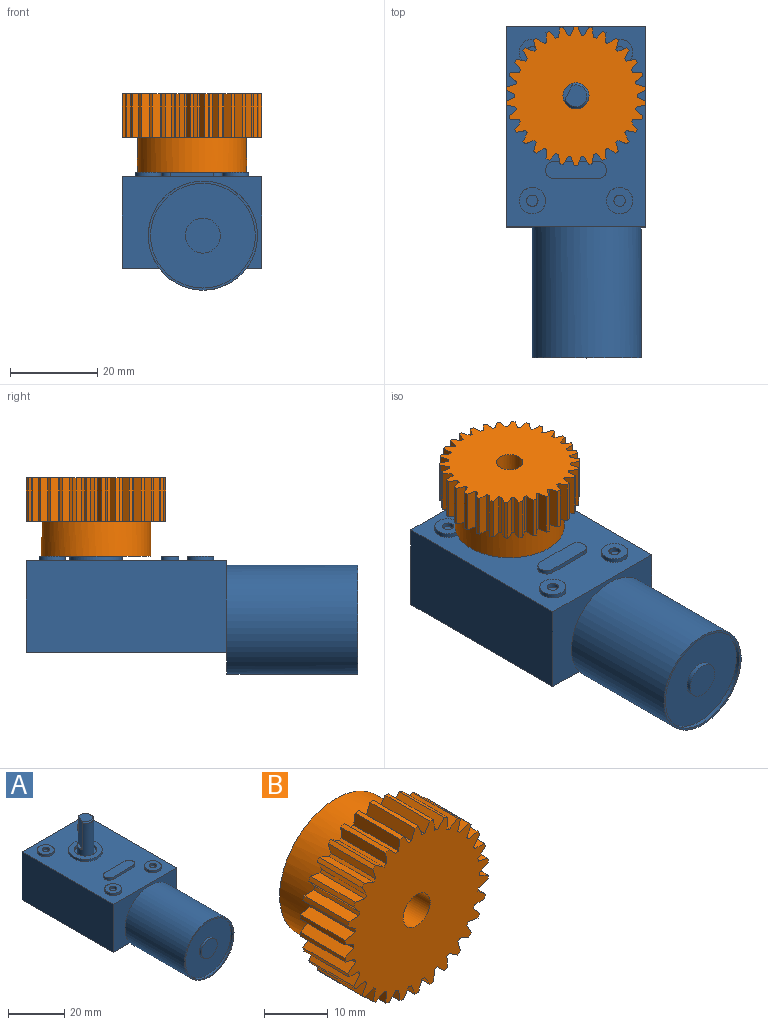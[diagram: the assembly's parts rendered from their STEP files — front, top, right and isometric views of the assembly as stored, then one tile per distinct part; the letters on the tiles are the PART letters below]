
ASSEMBLY  parts=2 mates=1
PART A: 43 faces, bbox 32.1x76.1x41.1 mm
  f0: plane 5x4.91mm, normal (0,0,1), area 18.3mm2, adj f1,f41
  f1: cone r=2.5mm half-angle=45deg, axis (0,0,-1), area 9.1mm2, adj f0,f40,f41
  f2: plane 46x32mm, normal (0,0,1), area 1193.2mm2, adj f10,f11,f13,f14,f16,f20,f24,f28
  f3: cylinder r=12.5mm len=30mm, axis (0,1,0), area 2356.2mm2, adj f4,f5,f10
  f4: plane 25x25mm, normal (0,-1,0), area 38.5mm2, adj f3,f7
  f5: plane 20x5mm, normal (0,1,0), area 69.9mm2, adj f3,f12
  f6: cylinder r=4mm len=8mm, axis (0,-1,0), area 25.1mm2, adj f8,f9
  f7: cylinder r=12mm len=24mm, axis (0,-1,0), area 75.4mm2, adj f4,f8
  f8: plane 24x24mm, normal (0,-1,0), area 402.1mm2, adj f6,f7
  f9: plane 8x8mm, normal (0,-1,0), area 50.3mm2, adj f6
  f10: plane 32x21mm, normal (0,-1,0), area 251mm2, adj f2,f3,f11,f12,f13
  f11: plane 46x21mm, normal (-1,0,0), area 966mm2, adj f2,f10,f12,f14
  f12: plane 46x32mm, normal (0,0,-1), area 1472mm2, adj f5,f10,f11,f13,f14
  f13: plane 46x21mm, normal (1,0,0), area 966mm2, adj f2,f10,f12,f14
  f14: plane 32x21mm, normal (0,1,0), area 672mm2, adj f2,f11,f12,f13
  f15: cylinder r=1.3mm len=2.6mm, axis (0,0,-1), area 8.2mm2, adj f17,f18
  f16: cylinder r=3mm len=6mm, axis (0,0,-1), area 18.8mm2, adj f2,f17
  f17: plane 6x6mm, normal (0,0,1), area 23mm2, adj f15,f16
  f18: plane 2.6x2.6mm, normal (0,0,1), area 5.3mm2, adj f15
  f19: cylinder r=1.3mm len=2.6mm, axis (0,0,-1), area 8.2mm2, adj f21,f22
  f20: cylinder r=3mm len=6mm, axis (0,0,-1), area 18.8mm2, adj f2,f21
  f21: plane 6x6mm, normal (0,0,1), area 23mm2, adj f19,f20
  f22: plane 2.6x2.6mm, normal (0,0,1), area 5.3mm2, adj f19
  f23: cylinder r=1.3mm len=2.6mm, axis (0,0,-1), area 8.2mm2, adj f25,f26
  f24: cylinder r=3mm len=6mm, axis (0,0,-1), area 18.8mm2, adj f2,f25
  f25: plane 6x6mm, normal (0,0,1), area 23mm2, adj f23,f24
  f26: plane 2.6x2.6mm, normal (0,0,1), area 5.3mm2, adj f23
  f27: cylinder r=1.3mm len=2.6mm, axis (0,0,-1), area 8.2mm2, adj f29,f30
  f28: cylinder r=3mm len=6mm, axis (0,0,-1), area 18.8mm2, adj f2,f29
  f29: plane 6x6mm, normal (0,0,1), area 23mm2, adj f27,f28
  f30: plane 2.6x2.6mm, normal (0,0,1), area 5.3mm2, adj f27
  f31: cylinder r=4mm len=8mm, axis (0,0,-1), area 25.1mm2, adj f33,f34
  f32: cylinder r=6mm len=12mm, axis (0,0,-1), area 37.7mm2, adj f2,f33
  f33: plane 12x12mm, normal (0,0,1), area 62.8mm2, adj f31,f32
  f34: plane 8x8mm, normal (0,0,1), area 22mm2, adj f31,f40
  f35: plane 10x1mm, normal (0,1,0), area 10mm2, adj f2,f36,f38,f39
  f36: cylinder r=2mm len=4mm, axis (0,0,-1), area 6.3mm2, adj f2,f35,f37,f39
  f37: plane 10x1mm, normal (0,-1,0), area 10mm2, adj f2,f36,f38,f39
  f38: cylinder r=2mm len=4mm, axis (0,0,-1), area 6.3mm2, adj f2,f35,f37,f39
  f39: plane 14x4mm, normal (0,0,1), area 52.6mm2, adj f35,f36,f37,f38
  f40: cylinder r=3mm len=14.5mm, axis (0,0,-1), area 211.9mm2, adj f1,f34,f41,f42
  f41: plane 12.06x4.26mm, normal (-0.9,0.43,0), area 55.6mm2, adj f0,f1,f40,f42
  f42: plane 4.21x2.31mm, normal (0,0,1), area 3.6mm2, adj f40,f41
PART B: 125 faces, bbox 31.9x18x32 mm
  f0: cylinder r=16mm len=10mm, axis (0,1,0), area 8.1mm2, adj f1,f119,f120,f121
  f1: plane 10x2.04mm, normal (-0.94,0,0.34), area 21.7mm2, adj f0,f2,f120,f121
  f2: cylinder r=14mm len=10mm, axis (0,1,0), area 6.4mm2, adj f1,f3,f120,f121
  f3: plane 10x1.84mm, normal (0.85,0,0.53), area 21.7mm2, adj f2,f4,f120,f121
  f4: cylinder r=16mm len=10mm, axis (0,1,0), area 8.1mm2, adj f3,f5,f120,f121
  f5: plane 10x2.15mm, normal (-0.99,0,0.14), area 21.7mm2, adj f4,f6,f120,f121
  f6: cylinder r=14mm len=10mm, axis (0,1,0), area 6.4mm2, adj f5,f7,f120,f121
  f7: plane 10x1.56mm, normal (0.72,0,0.69), area 21.7mm2, adj f6,f8,f120,f121
  f8: cylinder r=16mm len=10mm, axis (0,1,0), area 8.1mm2, adj f7,f9,f120,f121
  f9: plane 10x2.17mm, normal (-1,0,-0.07), area 21.7mm2, adj f8,f10,f120,f121
  f10: cylinder r=14mm len=10mm, axis (0,1,0), area 6.4mm2, adj f9,f11,f120,f121
  f11: plane 10x1.8mm, normal (0.56,0,0.83), area 21.7mm2, adj f10,f12,f120,f121
  f12: cylinder r=16mm len=10mm, axis (0,1,0), area 8.1mm2, adj f11,f13,f120,f121
  f13: plane 10x2.09mm, normal (-0.96,0,-0.28), area 21.7mm2, adj f12,f14,f120,f121
  f14: cylinder r=14mm len=10mm, axis (0,1,0), area 6.4mm2, adj f13,f15,f120,f121
  f15: plane 10x2.01mm, normal (0.38,0,0.93), area 21.7mm2, adj f14,f16,f120,f121
  f16: cylinder r=16mm len=10mm, axis (0,1,0), area 8.1mm2, adj f15,f17,f120,f121
  f17: plane 10x1.92mm, normal (-0.88,0,-0.47), area 21.7mm2, adj f16,f18,f120,f121
  f18: cylinder r=14mm len=10mm, axis (0,1,0), area 6.4mm2, adj f17,f19,f120,f121
  f19: plane 10x2.14mm, normal (0.17,0,0.98), area 21.7mm2, adj f18,f20,f120,f121
  f20: cylinder r=16mm len=10mm, axis (0,1,0), area 8.1mm2, adj f19,f21,f120,f121
  f21: plane 10x1.66mm, normal (-0.77,0,-0.64), area 21.7mm2, adj f20,f22,f120,f121
  f22: cylinder r=14mm len=10mm, axis (0,1,0), area 6.4mm2, adj f21,f23,f120,f121
  f23: plane 10x2.17mm, normal (-0.03,0,1), area 21.7mm2, adj f22,f24,f120,f121
  f24: cylinder r=16mm len=10mm, axis (0,1,0), area 8.1mm2, adj f23,f25,f120,f121
  f25: plane 10x1.71mm, normal (-0.61,0,-0.79), area 21.7mm2, adj f24,f26,f120,f121
  f26: cylinder r=14mm len=10mm, axis (0,1,0), area 6.4mm2, adj f25,f27,f120,f121
  f27: plane 10x2.11mm, normal (-0.24,0,0.97), area 21.7mm2, adj f26,f28,f120,f121
  f28: cylinder r=16mm len=10mm, axis (0,1,0), area 8.1mm2, adj f27,f29,f120,f121
  f29: plane 10x1.95mm, normal (-0.44,0,-0.9), area 21.7mm2, adj f28,f30,f120,f121
  f30: cylinder r=14mm len=10mm, axis (0,1,0), area 6.4mm2, adj f29,f31,f120,f121
  f31: plane 10x1.95mm, normal (-0.44,0,0.9), area 21.7mm2, adj f30,f32,f120,f121
  f32: cylinder r=16mm len=10mm, axis (0,1,0), area 8.1mm2, adj f31,f33,f120,f121
  f33: plane 10x2.11mm, normal (-0.24,0,-0.97), area 21.7mm2, adj f32,f34,f120,f121
  f34: cylinder r=14mm len=10mm, axis (0,1,0), area 6.4mm2, adj f33,f35,f120,f121
  f35: plane 10x1.71mm, normal (-0.61,0,0.79), area 21.7mm2, adj f34,f36,f120,f121
  f36: cylinder r=16mm len=10mm, axis (0,1,0), area 8.1mm2, adj f35,f37,f120,f121
  f37: plane 10x2.17mm, normal (-0.03,0,-1), area 21.7mm2, adj f36,f38,f120,f121
  f38: cylinder r=14mm len=10mm, axis (0,1,0), area 6.4mm2, adj f37,f39,f120,f121
  f39: plane 10x1.66mm, normal (-0.77,0,0.64), area 21.7mm2, adj f38,f40,f120,f121
  f40: cylinder r=16mm len=10mm, axis (0,1,0), area 8.1mm2, adj f39,f41,f120,f121
  f41: plane 10x2.14mm, normal (0.17,0,-0.98), area 21.7mm2, adj f40,f42,f120,f121
  f42: cylinder r=14mm len=10mm, axis (0,1,0), area 6.4mm2, adj f41,f43,f120,f121
  f43: plane 10x1.92mm, normal (-0.88,0,0.47), area 21.7mm2, adj f42,f44,f120,f121
  f44: cylinder r=16mm len=10mm, axis (0,1,0), area 8.1mm2, adj f43,f45,f120,f121
  f45: plane 10x2.01mm, normal (0.38,0,-0.93), area 21.7mm2, adj f44,f46,f120,f121
  f46: cylinder r=14mm len=10mm, axis (0,1,0), area 6.4mm2, adj f45,f47,f120,f121
  f47: plane 10x2.09mm, normal (-0.96,0,0.28), area 21.7mm2, adj f46,f48,f120,f121
  f48: cylinder r=16mm len=10mm, axis (0,1,0), area 8.1mm2, adj f47,f49,f120,f121
  f49: plane 10x1.8mm, normal (0.56,0,-0.83), area 21.7mm2, adj f48,f50,f120,f121
  f50: cylinder r=14mm len=10mm, axis (0,1,0), area 6.4mm2, adj f49,f51,f120,f121
  f51: plane 10x2.17mm, normal (-1,0,0.07), area 21.7mm2, adj f50,f52,f120,f121
  f52: cylinder r=16mm len=10mm, axis (0,1,0), area 8.1mm2, adj f51,f53,f120,f121
  f53: plane 10x1.56mm, normal (0.72,0,-0.69), area 21.7mm2, adj f52,f54,f120,f121
  f54: cylinder r=14mm len=10mm, axis (0,1,0), area 6.4mm2, adj f53,f55,f120,f121
  f55: plane 10x2.15mm, normal (-0.99,0,-0.14), area 21.7mm2, adj f54,f56,f120,f121
  f56: cylinder r=16mm len=10mm, axis (0,1,0), area 8.1mm2, adj f55,f57,f120,f121
  f57: plane 10x1.84mm, normal (0.85,0,-0.53), area 21.7mm2, adj f56,f58,f120,f121
  f58: cylinder r=14mm len=10mm, axis (0,1,0), area 6.4mm2, adj f57,f59,f120,f121
  f59: plane 10x2.04mm, normal (-0.94,0,-0.34), area 21.7mm2, adj f58,f60,f120,f121
  f60: cylinder r=16mm len=10mm, axis (0,1,0), area 8.1mm2, adj f59,f61,f120,f121
  f61: plane 10x2.04mm, normal (0.94,0,-0.34), area 21.7mm2, adj f60,f62,f120,f121
  f62: cylinder r=14mm len=10mm, axis (0,1,0), area 6.4mm2, adj f61,f63,f120,f121
  f63: plane 10x1.84mm, normal (-0.85,0,-0.53), area 21.7mm2, adj f62,f64,f120,f121
  f64: cylinder r=16mm len=10mm, axis (0,1,0), area 8.1mm2, adj f63,f65,f120,f121
  f65: plane 10x2.15mm, normal (0.99,0,-0.14), area 21.7mm2, adj f64,f66,f120,f121
  f66: cylinder r=14mm len=10mm, axis (0,1,0), area 6.4mm2, adj f65,f67,f120,f121
  f67: plane 10x1.56mm, normal (-0.72,0,-0.69), area 21.7mm2, adj f66,f68,f120,f121
  f68: cylinder r=16mm len=10mm, axis (0,1,0), area 8.1mm2, adj f67,f69,f120,f121
  f69: plane 10x2.17mm, normal (1,0,0.07), area 21.7mm2, adj f68,f70,f120,f121
  f70: cylinder r=14mm len=10mm, axis (0,1,0), area 6.4mm2, adj f69,f71,f120,f121
  f71: plane 10x1.8mm, normal (-0.56,0,-0.83), area 21.7mm2, adj f70,f72,f120,f121
  f72: cylinder r=16mm len=10mm, axis (0,1,0), area 8.1mm2, adj f71,f73,f120,f121
  f73: plane 10x2.09mm, normal (0.96,0,0.28), area 21.7mm2, adj f72,f74,f120,f121
  f74: cylinder r=14mm len=10mm, axis (0,1,0), area 6.4mm2, adj f73,f75,f120,f121
  f75: plane 10x2.01mm, normal (-0.38,0,-0.93), area 21.7mm2, adj f74,f76,f120,f121
  f76: cylinder r=16mm len=10mm, axis (0,1,0), area 8.1mm2, adj f75,f77,f120,f121
  f77: plane 10x1.92mm, normal (0.88,0,0.47), area 21.7mm2, adj f76,f78,f120,f121
  f78: cylinder r=14mm len=10mm, axis (0,1,0), area 6.4mm2, adj f77,f79,f120,f121
  f79: plane 10x2.14mm, normal (-0.17,0,-0.98), area 21.7mm2, adj f78,f80,f120,f121
  f80: cylinder r=16mm len=10mm, axis (0,1,0), area 8.1mm2, adj f79,f81,f120,f121
  f81: plane 10x1.66mm, normal (0.77,0,0.64), area 21.7mm2, adj f80,f82,f120,f121
  f82: cylinder r=14mm len=10mm, axis (0,1,0), area 6.4mm2, adj f81,f83,f120,f121
  f83: plane 10x2.17mm, normal (0.03,0,-1), area 21.7mm2, adj f82,f84,f120,f121
  f84: cylinder r=16mm len=10mm, axis (0,1,0), area 8.1mm2, adj f83,f85,f120,f121
  f85: plane 10x1.71mm, normal (0.61,0,0.79), area 21.7mm2, adj f84,f86,f120,f121
  f86: cylinder r=14mm len=10mm, axis (0,1,0), area 6.4mm2, adj f85,f87,f120,f121
  f87: plane 10x2.11mm, normal (0.24,0,-0.97), area 21.7mm2, adj f86,f88,f120,f121
  f88: cylinder r=16mm len=10mm, axis (0,1,0), area 8.1mm2, adj f87,f89,f120,f121
  f89: plane 10x1.95mm, normal (0.44,0,0.9), area 21.7mm2, adj f88,f90,f120,f121
  f90: cylinder r=14mm len=10mm, axis (0,1,0), area 6.4mm2, adj f89,f91,f120,f121
  f91: plane 10x1.95mm, normal (0.44,0,-0.9), area 21.7mm2, adj f90,f92,f120,f121
  f92: cylinder r=16mm len=10mm, axis (0,1,0), area 8.1mm2, adj f91,f93,f120,f121
  f93: plane 10x2.11mm, normal (0.24,0,0.97), area 21.7mm2, adj f92,f94,f120,f121
  f94: cylinder r=14mm len=10mm, axis (0,1,0), area 6.4mm2, adj f93,f95,f120,f121
  f95: plane 10x1.71mm, normal (0.61,0,-0.79), area 21.7mm2, adj f94,f96,f120,f121
  f96: cylinder r=16mm len=10mm, axis (0,1,0), area 8.1mm2, adj f95,f97,f120,f121
  f97: plane 10x2.17mm, normal (0.03,0,1), area 21.7mm2, adj f96,f98,f120,f121
  f98: cylinder r=14mm len=10mm, axis (0,1,0), area 6.4mm2, adj f97,f99,f120,f121
  f99: plane 10x1.66mm, normal (0.77,0,-0.64), area 21.7mm2, adj f98,f100,f120,f121
  f100: cylinder r=16mm len=10mm, axis (0,1,0), area 8.1mm2, adj f99,f101,f120,f121
  f101: plane 10x2.14mm, normal (-0.17,0,0.98), area 21.7mm2, adj f100,f102,f120,f121
  f102: cylinder r=14mm len=10mm, axis (0,1,0), area 6.4mm2, adj f101,f103,f120,f121
  f103: plane 10x1.92mm, normal (0.88,0,-0.47), area 21.7mm2, adj f102,f104,f120,f121
  f104: cylinder r=16mm len=10mm, axis (0,1,0), area 8.1mm2, adj f103,f105,f120,f121
  f105: plane 10x2.01mm, normal (-0.38,0,0.93), area 21.7mm2, adj f104,f106,f120,f121
  f106: cylinder r=14mm len=10mm, axis (0,1,0), area 6.4mm2, adj f105,f107,f120,f121
  f107: plane 10x2.09mm, normal (0.96,0,-0.28), area 21.7mm2, adj f106,f108,f120,f121
  f108: cylinder r=16mm len=10mm, axis (0,1,0), area 8.1mm2, adj f107,f109,f120,f121
  f109: plane 10x1.8mm, normal (-0.56,0,0.83), area 21.7mm2, adj f108,f110,f120,f121
  f110: cylinder r=14mm len=10mm, axis (0,1,0), area 6.4mm2, adj f109,f111,f120,f121
  f111: plane 10x2.17mm, normal (1,0,-0.07), area 21.7mm2, adj f110,f112,f120,f121
  f112: cylinder r=16mm len=10mm, axis (0,1,0), area 8.1mm2, adj f111,f113,f120,f121
  f113: plane 10x1.56mm, normal (-0.72,0,0.69), area 21.7mm2, adj f112,f114,f120,f121
  f114: cylinder r=14mm len=10mm, axis (0,1,0), area 6.4mm2, adj f113,f115,f120,f121
  f115: plane 10x2.15mm, normal (0.99,0,0.14), area 21.7mm2, adj f114,f116,f120,f121
  f116: cylinder r=16mm len=10mm, axis (0,1,0), area 8.1mm2, adj f115,f117,f120,f121
  f117: plane 10x1.84mm, normal (-0.85,0,0.53), area 21.7mm2, adj f116,f118,f120,f121
  f118: cylinder r=14mm len=10mm, axis (0,1,0), area 6.4mm2, adj f117,f119,f120,f121
  f119: plane 10x2.04mm, normal (0.94,0,0.34), area 21.7mm2, adj f0,f118,f120,f121
  f120: plane 32x31.9mm, normal (0,-1,0), area 680.4mm2, adj f0,f1,f2,f3,f4,f5,f6,f7
  f121: plane 32x31.9mm, normal (0,1,0), area 217.8mm2, adj f0,f1,f2,f3,f4,f5,f6,f7
  f122: cylinder r=12.5mm len=25mm, axis (0,-1,0), area 628.3mm2, adj f121,f123
  f123: plane 25x25mm, normal (0,1,0), area 462.6mm2, adj f122,f124
  f124: cylinder r=3mm len=18mm, axis (0,1,0), area 339.3mm2, adj f120,f123
PLACE A t=(-16.13,-14.01,-0.87)mm
PLACE B rot(axis=(-1,0,0),90deg) t=(-18.63,15.99,21.63)mm
MATE revolute B.f122 <-> A.f1  axis (0,0,-1) through (-18.63,15.99,13.63)mm
